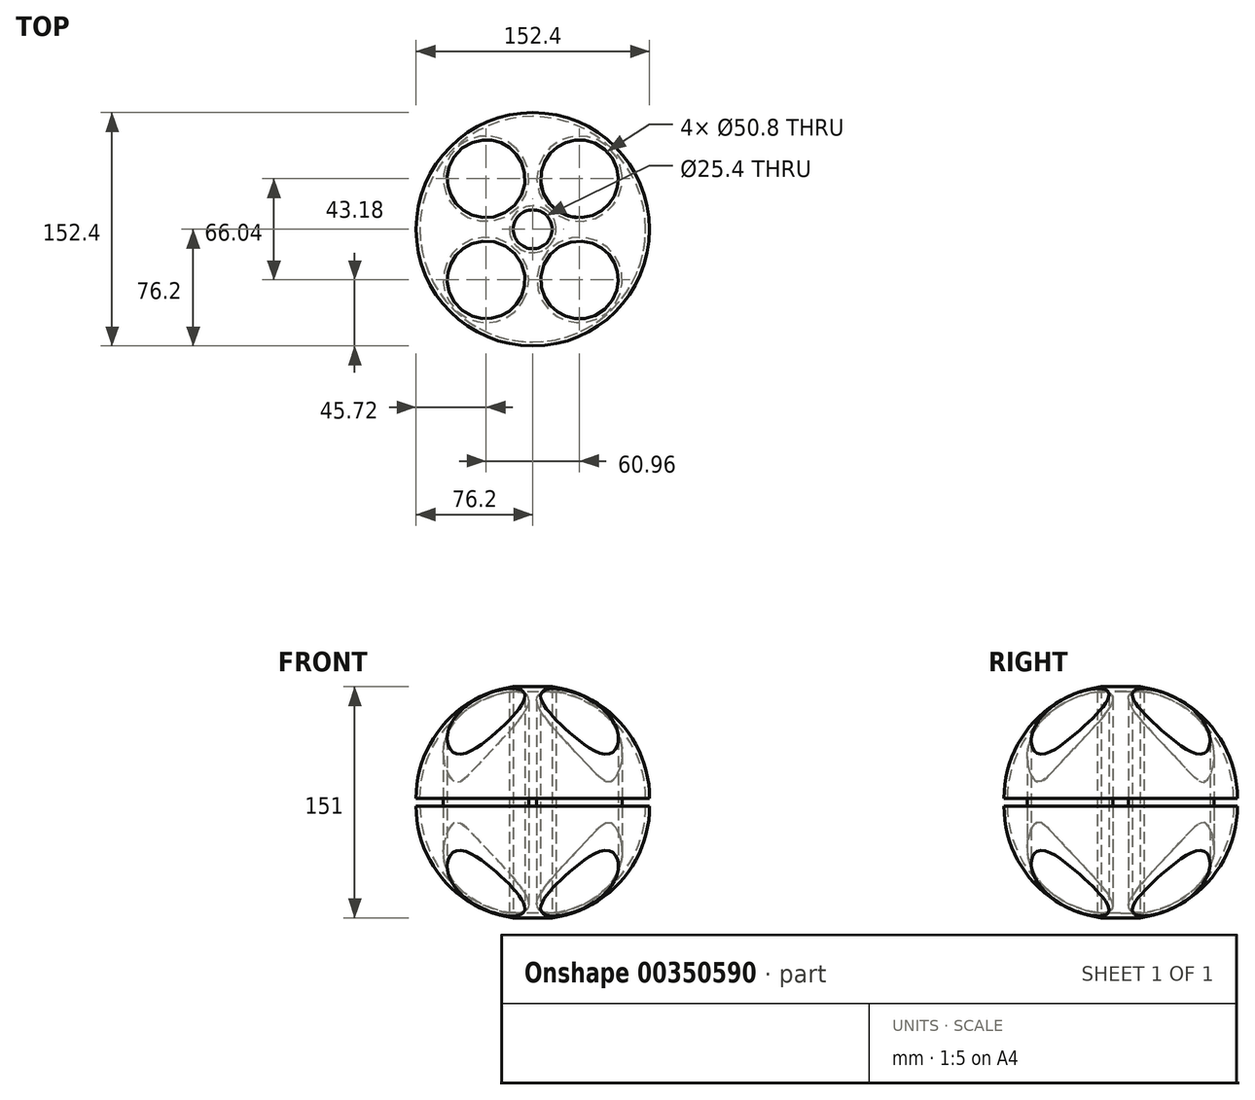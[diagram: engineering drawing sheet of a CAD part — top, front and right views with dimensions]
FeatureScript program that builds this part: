
annotation { "Feature Type Name" : "Feature", "Feature Type Description" : "" }
export const myFeature = defineFeature(function(context is Context, id is Id, definition is map)
    precondition{}
    {
        {
            var Q0;
            Q0=qCreatedBy(makeId("Top.planeOp"),FACE);
            var sketch = newSketch(context, id + "F0", { "sketchPlane" : qUnion([Q0])});
            skEllipse(sketch, "E0", {"center": v(0, 0) * mm, "majorRadius": 76.2 * mm, "minorRadius": 76.2 * mm, "majorAxis": v(0, 1)});
            skCircle(sketch, "E1", {"center": v(-30.48, 33.02) * mm, "radius": 25.4 * mm});
            skLineSegment(sketch, "E2", {"start": v(0, 76.2) * mm, "end": v(0, -76.2) * mm});
            skLineSegment(sketch, "E3", {"start": v(-76.2, 0) * mm, "end": v(76.2, 0) * mm});
            skCircle(sketch, "E4", {"center": v(30.48, 33.02) * mm, "radius": 25.4 * mm});
            skCircle(sketch, "E5", {"center": v(-30.48, -33.02) * mm, "radius": 25.4 * mm});
            skCircle(sketch, "E6", {"center": v(30.48, -33.02) * mm, "radius": 25.4 * mm});
            skPoint(sketch, "E7", {"position": v(-30.48, 0) * mm});
            skSolve(sketch);
        }
        {
            var Q0;
            Q0 = qSketchRegion(id + "F0", true);
            extrude(context, id + "F1", {"entities" : qUnion([Q0]), "depth" : 152.4 * mm});
        }
        {
            var Q0;
            Q0=makeQuery(id+"F1.opExtrude","CAP_EDGE",EDGE,{"disambiguationData":[OSD([sQuery(id+"F0.wireOp",EDGE,"E0")])],"isStart":false});
            fillet(context, id + "F2", {"entities" : qUnion([Q0]), "radius" : 73.66 * mm, "tangentPropagation" : true, "allowEdgeOverflow" : false});
        }
        {
            var Q0;
            Q0=makeQuery(id+"F1.opExtrude","CAP_EDGE",EDGE,{"disambiguationData":[OSD([sQuery(id+"F0.wireOp",EDGE,"E0")])],"isStart":true});
            fillet(context, id + "F3", {"entities" : qUnion([Q0]), "radius" : 73.66 * mm, "tangentPropagation" : true, "allowEdgeOverflow" : false});
        }
        {
            var Q0;
            Q0=sQuery(id+"F0.wireOp",VERTEX,"E0.center");
            var Q1;
            Q1=makeQuery(id+"F1.opExtrude","SWEPT_BODY",BODY,{"disambiguationData":[OSD([sQuery(id+"F0.wireOp",EDGE,"E0"),sQuery(id+"F0.wireOp",EDGE,"E1"),sQuery(id+"F0.wireOp",EDGE,"E4"),sQuery(id+"F0.wireOp",EDGE,"E5"),sQuery(id+"F0.wireOp",EDGE,"E6")])]});
            hole(context, id + "F4", {"style" : HoleStyle.C_BORE, "endStyle" : HoleEndStyle.THROUGH, "oppositeDirection" : true, "holeDiameter" : 25.4 * mm, "cBoreDiameter" : 25.4 * mm, "cBoreDepth" : 6.35 * mm, "isTappedThrough" : true, "tappedDepth" : 12.7 * mm, "tapClearance" : 3, "locations" : qUnion([Q0]), "scope" : qUnion([Q1])});
        }
        {
            var Q0;
            Q0=makeQuery(id+"F1.opExtrude","SWEPT_FACE",FACE,{"disambiguationData":[OSD([sQuery(id+"F0.wireOp",EDGE,"E0")])]});
            shell(context, id + "F5", {"entities" : qUnion([Q0]), "thickness" : 2.54 * mm});
        }
    });
